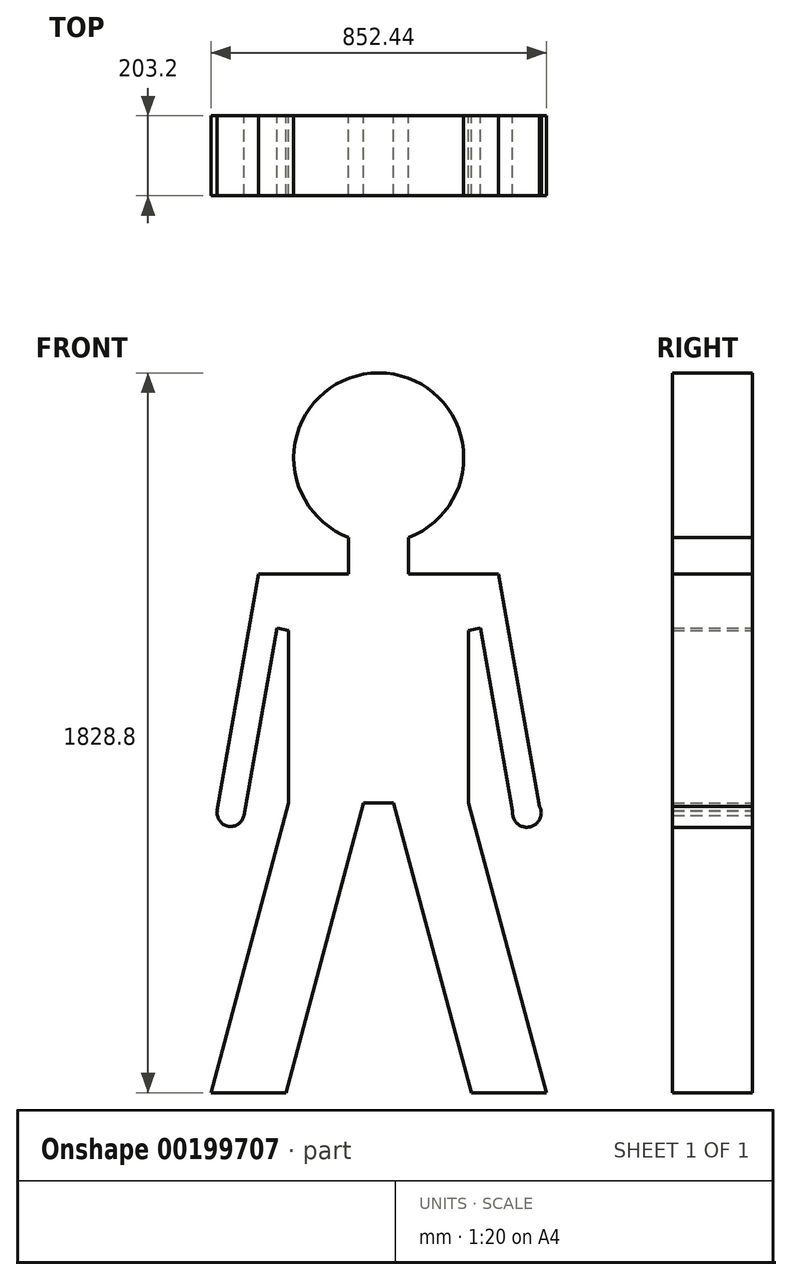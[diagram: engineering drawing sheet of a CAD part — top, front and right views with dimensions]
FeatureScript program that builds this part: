
annotation { "Feature Type Name" : "Feature", "Feature Type Description" : "" }
export const myFeature = defineFeature(function(context is Context, id is Id, definition is map)
    precondition{}
    {
        {
            var Q0;
            Q0=qCreatedBy(makeId("Front.planeOp"),FACE);
            var sketch = newSketch(context, id + "F0", { "sketchPlane" : qUnion([Q0])});
            skLineSegment(sketch, "E0", {"start": v(0, 0) * mm, "end": v(0, 1828.8) * mm, "construction": true});
            skArc(sketch, "E1", {"start": v(76.2, 1410.9) * mm, "mid": v(0, 1828.8) * mm, "end": v(-76.2, 1410.9) * mm});
            skLineSegment(sketch, "E2.left", {"start": v(-76.2, 1410.9) * mm, "end": v(-76.2, 1317.27) * mm});
            skLineSegment(sketch, "E2.right", {"start": v(76.2, 1410.9) * mm, "end": v(76.2, 1317.27) * mm});
            skLineSegment(sketch, "E3.bottom", {"start": v(-228.6, 1317.27) * mm, "end": v(-76.2, 1317.27) * mm});
            skLineSegment(sketch, "E3.left", {"start": v(-228.6, 1174.87) * mm, "end": v(-228.6, 863.18) * mm});
            skLineSegment(sketch, "E3.right", {"start": v(228.6, 1174.87) * mm, "end": v(228.6, 863.18) * mm});
            skLineSegment(sketch, "E4", {"start": v(-228.6, 863.18) * mm, "end": v(-228.6, 735.93) * mm});
            skLineSegment(sketch, "E5", {"start": v(-228.6, 735.93) * mm, "end": v(-426.22, 0) * mm});
            skLineSegment(sketch, "E6", {"start": v(-426.22, 0) * mm, "end": v(-235.72, 0) * mm});
            skLineSegment(sketch, "E7", {"start": v(-235.72, 0) * mm, "end": v(-38.1, 735.93) * mm});
            skLineSegment(sketch, "E8", {"start": v(-38.1, 735.93) * mm, "end": v(38.1, 735.93) * mm});
            skLineSegment(sketch, "E9", {"start": v(38.1, 735.93) * mm, "end": v(235.72, 0) * mm});
            skLineSegment(sketch, "E10", {"start": v(235.72, 0) * mm, "end": v(426.22, 0) * mm});
            skLineSegment(sketch, "E11", {"start": v(426.22, 0) * mm, "end": v(228.6, 735.93) * mm});
            skLineSegment(sketch, "E12", {"start": v(228.6, 735.93) * mm, "end": v(228.6, 863.18) * mm});
            skLineSegment(sketch, "E13.trimOffspring", {"start": v(76.2, 1317.27) * mm, "end": v(228.6, 1317.27) * mm});
            skLineSegment(sketch, "E14", {"start": v(-228.6, 1317.27) * mm, "end": v(-304.8, 1317.27) * mm});
            skLineSegment(sketch, "E15", {"start": v(-304.8, 1317.27) * mm, "end": v(-410.66, 716.93) * mm});
            skLineSegment(sketch, "E16", {"start": v(228.6, 1317.27) * mm, "end": v(304.8, 1317.27) * mm});
            skLineSegment(sketch, "E17", {"start": v(304.8, 1317.27) * mm, "end": v(408.8, 727.5) * mm});
            skLineSegment(sketch, "E18", {"start": v(-410.66, 716.93) * mm, "end": v(-410.12, 716.83) * mm});
            skLineSegment(sketch, "E19", {"start": v(-341.9, 704.8) * mm, "end": v(-258.1, 1180.08) * mm});
            skLineSegment(sketch, "E20", {"start": v(-258.1, 1180.08) * mm, "end": v(-228.6, 1174.87) * mm});
            skLineSegment(sketch, "E21", {"start": v(228.6, 1174.87) * mm, "end": v(258.1, 1180.08) * mm});
            skLineSegment(sketch, "E22", {"start": v(258.1, 1180.08) * mm, "end": v(340.04, 715.38) * mm});
            skArc(sketch, "E23", {"start": v(-410.12, 716.83) * mm, "mid": v(-382.25, 677.03) * mm, "end": v(-342.44, 704.9) * mm});
            skArc(sketch, "E24", {"start": v(340.04, 715.38) * mm, "mid": v(382.62, 674.9) * mm, "end": v(408.8, 727.5) * mm});
            skLineSegment(sketch, "E25.trimOffspring", {"start": v(-342.44, 704.9) * mm, "end": v(-341.9, 704.8) * mm});
            skPoint(sketch, "E26.orphan", {"position": v(341.9, 704.8) * mm});
            skPoint(sketch, "E27.orphan", {"position": v(410.66, 716.93) * mm});
            skSolve(sketch);
        }
        {
            var Q0;
            Q0=makeQuery(id+"F0.imprint","IMPRINT",FACE,{"disambiguationData":[TD([[makeQuery(id+"F0.imprint","IMPRINT",EDGE,{"derivedFrom":sQuery(id+"F0.wireOp",EDGE,"E1")}),1.0]])]});
            extrude(context, id + "F1", {"entities" : qUnion([Q0]), "depth" : 203.2 * mm});
        }
    });
